# Revit family: Bath-Freestanding-KOHLER-Imperator-K-8334
name_source: partatom
category: Plumbing Fixtures
revit_build: Autodesk Revit 2015 (Build: 20140606_1530(x64)
units: mm (PartAtom-declared; Revit-internal decimal feet)

## types (1)
- 0-White
    ADA Compliant = No
    Assembly Code = D2010500
    CW Connection = No
    Cold Water Inlet = Cold Water Inlet
    Date Modified = 01/04/2019
    Default Elevation = 0"
    Description = 66inch x 31inch freestanding bath with center toe-tap drain
    Drain Included = Yes
    Finish = Kohler-Lithocast-0-White
    HW Connection = No
    Height = 23 3/4"
    Hot Water Inlet = Hot Water Inlet
    Length = 65 3/4"
    Manufacturer = KOHLER Co.
    MasterFormat 1995 = 15410
    MasterFormat 2004 = 22.41.19
    Material = Lithocast Gloss Cast Resin
    Model = K-8334-0
    Product Documentation Link = http://www.us.kohler.com
    Product Name = Imperator
    Product Page URL = http://www.us.kohler.com
    URL = https://www.us.kohler.com
    Vent Connection = No
    Waste Connection = Yes
    Waste Water Outlet = Waste Water Outlet
    Width = 30 15/16"

## geometry (parser evidence)
native form markers: Sweep x4
no freeform markers — native parametric forms only
